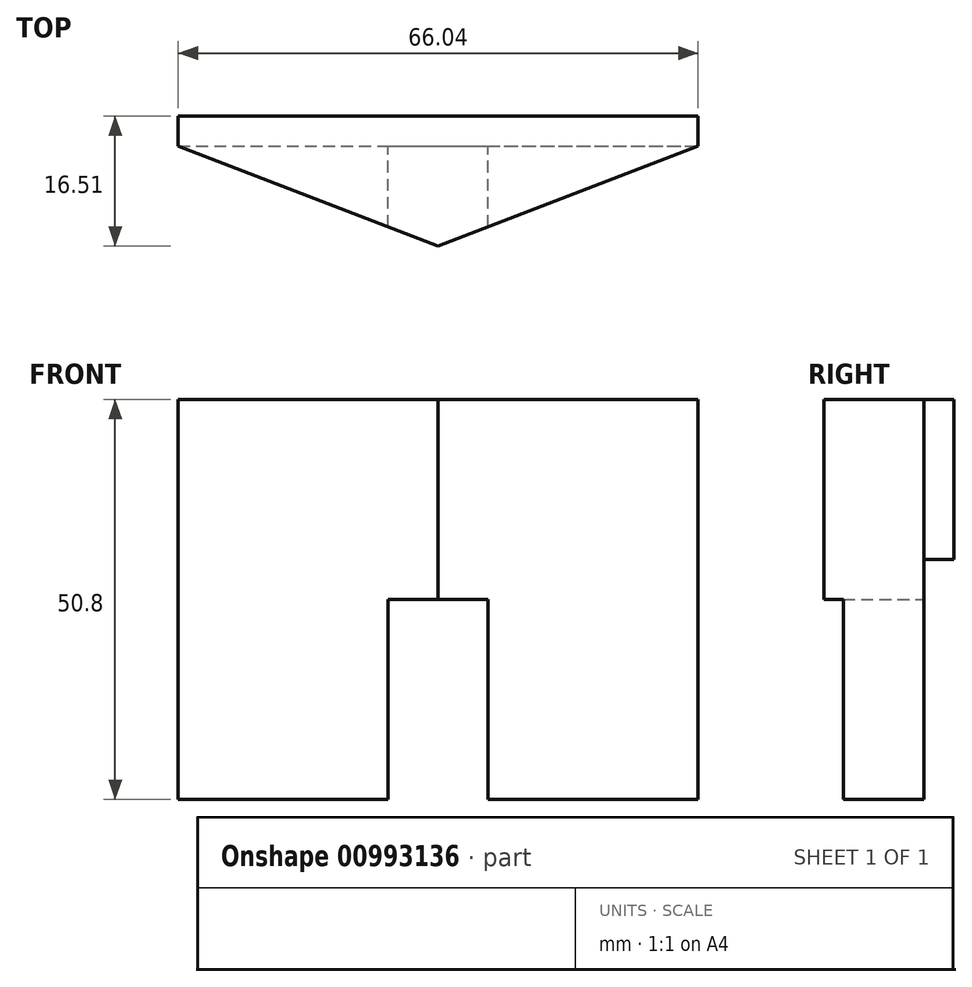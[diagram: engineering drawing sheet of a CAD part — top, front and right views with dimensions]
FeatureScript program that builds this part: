
annotation { "Feature Type Name" : "Feature", "Feature Type Description" : "" }
export const myFeature = defineFeature(function(context is Context, id is Id, definition is map)
    precondition{}
    {
        {
            var Q0;
            Q0=qCreatedBy(makeId("Top.planeOp"),FACE);
            var sketch = newSketch(context, id + "F0", { "sketchPlane" : qUnion([Q0])});
            skLineSegment(sketch, "E0", {"start": v(-69.43, -25.75) * mm, "end": v(-3.4, -25.75) * mm});
            skLineSegment(sketch, "E1", {"start": v(-36.41, -38.45) * mm, "end": v(-69.43, -25.75) * mm});
            skPoint(sketch, "E1.startSnap0", {"position": v(-36.41, -25.75) * mm});
            skLineSegment(sketch, "E2", {"start": v(-36.41, -38.45) * mm, "end": v(-3.4, -25.75) * mm});
            skSolve(sketch);
        }
        {
            var Q0;
            Q0=makeQuery(id+"F0.imprint","IMPRINT",FACE,{"disambiguationData":[TD([[makeQuery(id+"F0.imprint","IMPRINT",EDGE,{"derivedFrom":sQuery(id+"F0.wireOp",EDGE,"E0")}),-1.0]])]});
            extrude(context, id + "F1", {"entities" : qUnion([Q0]), "depth" : 50.8 * mm, "offsetDistance" : 25.4 * mm});
        }
        {
            var Q0;
            Q0=makeQuery(id+"F1.opExtrude","SWEPT_FACE",FACE,{"disambiguationData":[OSD([sQuery(id+"F0.wireOp",EDGE,"E0")])]});
            var sketch = newSketch(context, id + "F2", { "sketchPlane" : qUnion([Q0])});
            skPoint(sketch, "E3.startSnap0", {"position": v(36.41, 50.8) * mm});
            skLineSegment(sketch, "E4.bottom", {"start": v(42.76, 25.4) * mm, "end": v(30.06, 25.4) * mm});
            skLineSegment(sketch, "E4.top", {"start": v(42.76, 0) * mm, "end": v(30.06, 0) * mm});
            skLineSegment(sketch, "E4.left", {"start": v(42.76, 25.4) * mm, "end": v(42.76, 0) * mm});
            skLineSegment(sketch, "E4.right", {"start": v(30.06, 25.4) * mm, "end": v(30.06, 0) * mm});
            skSolve(sketch);
        }
        {
            var Q0;
            {var subQ0=sQuery(id+"F2.wireOp",EDGE,"E3");Q0=makeQuery(id+"F2.imprint","IMPRINT",FACE,{"disambiguationData":[TD([[makeQuery(id+"F2.imprint","IMPRINT",EDGE,{"derivedFrom":subQ0}),1.0]])]});}
            var Q1;
            Q1=makeQuery(id+"F2.imprint","IMPRINT",FACE,{"disambiguationData":[TD([[makeQuery(id+"F2.imprint","IMPRINT",EDGE,{"derivedFrom":sQuery(id+"F2.wireOp",EDGE,"E4.bottom")}),1.0]])]});
            extrude(context, id + "F3", {"entities" : qUnion([Q0, Q1]), "operationType" : NewBodyOperationType.REMOVE, "oppositeDirection" : true, "depth" : 25.4 * mm, "offsetDistance" : 25.4 * mm});
        }
        {
            var Q0;
            Q0=makeQuery(id+"F1.opExtrude","SWEPT_FACE",FACE,{"disambiguationData":[OSD([sQuery(id+"F0.wireOp",EDGE,"E0")])]});
            var sketch = newSketch(context, id + "F4", { "sketchPlane" : qUnion([Q0])});
            skLineSegment(sketch, "E5.bottom", {"start": v(69.43, 50.8) * mm, "end": v(3.4, 50.8) * mm});
            skLineSegment(sketch, "E5.top", {"start": v(69.43, 30.48) * mm, "end": v(3.4, 30.48) * mm});
            skLineSegment(sketch, "E5.left", {"start": v(69.43, 50.8) * mm, "end": v(69.43, 30.48) * mm});
            skLineSegment(sketch, "E5.right", {"start": v(3.4, 50.8) * mm, "end": v(3.4, 30.48) * mm});
            skSolve(sketch);
        }
        {
            var Q0;
            Q0=makeQuery(id+"F4.imprint","IMPRINT",FACE,{"disambiguationData":[TD([[makeQuery(id+"F4.imprint","IMPRINT",EDGE,{"derivedFrom":sQuery(id+"F4.wireOp",EDGE,"E5.bottom")}),1.0]])]});
            extrude(context, id + "F5", {"entities" : qUnion([Q0]), "operationType" : NewBodyOperationType.ADD, "depth" : 3.8 * mm, "offsetDistance" : 25.4 * mm});
        }
    });
